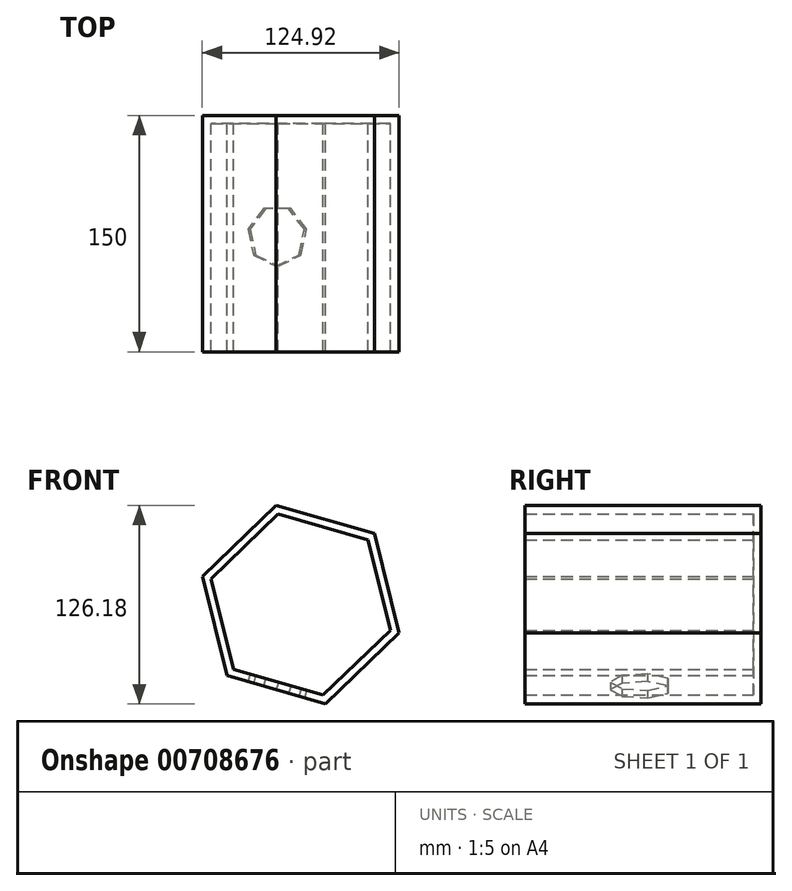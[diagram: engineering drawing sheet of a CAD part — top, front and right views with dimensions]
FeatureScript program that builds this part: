
annotation { "Feature Type Name" : "Feature", "Feature Type Description" : "" }
export const myFeature = defineFeature(function(context is Context, id is Id, definition is map)
    precondition{}
    {
        {
            var Q0;
            Q0=qCreatedBy(makeId("Front.planeOp"),FACE);
            var sketch = newSketch(context, id + "F0", { "sketchPlane" : qUnion([Q0])});
            skCircle(sketch, "E0.cCircle", {"center": v(3.4, 0) * mm, "radius": 56.3 * mm, "construction": true});
            skLineSegment(sketch, "E0.0", {"start": v(-59.06, 17.99) * mm, "end": v(-12.25, 63.09) * mm});
            skLineSegment(sketch, "E0.1", {"start": v(-12.25, 63.09) * mm, "end": v(50.21, 45.1) * mm});
            skLineSegment(sketch, "E0.2", {"start": v(50.21, 45.1) * mm, "end": v(65.86, -17.99) * mm});
            skLineSegment(sketch, "E0.3", {"start": v(65.86, -17.99) * mm, "end": v(19.05, -63.09) * mm});
            skLineSegment(sketch, "E0.4", {"start": v(19.05, -63.09) * mm, "end": v(-43.4, -45.1) * mm});
            skLineSegment(sketch, "E0.5", {"start": v(-43.4, -45.1) * mm, "end": v(-59.06, 17.99) * mm});
            skPoint(sketch, "E0.0.midPoint", {"position": v(-35.65, 40.54) * mm});
            skSolve(sketch);
        }
        {
            var Q0;
            Q0 = qSketchRegion(id + "F0", true);
            extrude(context, id + "F1", {"entities" : qUnion([Q0]), "depth" : 150 * mm, "offsetDistance" : 25.4 * mm});
        }
        {
            var Q0;
            Q0=makeQuery(id+"F1.opExtrude","CAP_FACE",FACE,{"disambiguationData":[OSD([sQuery(id+"F0.wireOp",EDGE,"E0.0"),sQuery(id+"F0.wireOp",EDGE,"E0.1"),sQuery(id+"F0.wireOp",EDGE,"E0.2"),sQuery(id+"F0.wireOp",EDGE,"E0.3"),sQuery(id+"F0.wireOp",EDGE,"E0.4"),sQuery(id+"F0.wireOp",EDGE,"E0.5")])],"isStart":false});
            shell(context, id + "F2", {"entities" : qUnion([Q0]), "thickness" : 5 * mm});
        }
        {
            var Q0;
            Q0=makeQuery(id+"F1.opExtrude","SWEPT_FACE",FACE,{"disambiguationData":[OSD([sQuery(id+"F0.wireOp",EDGE,"E0.4")])]});
            var sketch = newSketch(context, id + "F3", { "sketchPlane" : qUnion([Q0])});
            skCircle(sketch, "E1.cCircle", {"center": v(3.27, 76.46) * mm, "radius": 17.27 * mm, "construction": true});
            skPoint(sketch, "E1.cCircle.centerSnap0", {"position": v(3.27, 150) * mm});
            skLineSegment(sketch, "E1.0", {"start": v(11.59, 59.2) * mm, "end": v(-5.05, 59.2) * mm});
            skLineSegment(sketch, "E1.1", {"start": v(-5.05, 59.2) * mm, "end": v(-15.42, 72.2) * mm});
            skLineSegment(sketch, "E1.2", {"start": v(-15.42, 72.2) * mm, "end": v(-11.72, 88.42) * mm});
            skLineSegment(sketch, "E1.3", {"start": v(-11.72, 88.42) * mm, "end": v(3.27, 95.64) * mm});
            skLineSegment(sketch, "E1.4", {"start": v(3.27, 95.64) * mm, "end": v(18.26, 88.42) * mm});
            skLineSegment(sketch, "E1.5", {"start": v(18.26, 88.42) * mm, "end": v(21.96, 72.2) * mm});
            skLineSegment(sketch, "E1.6", {"start": v(21.96, 72.2) * mm, "end": v(11.59, 59.2) * mm});
            skPoint(sketch, "E1.0.midPoint", {"position": v(3.27, 59.2) * mm});
            skSolve(sketch);
        }
        {
            var Q0;
            Q0 = qSketchRegion(id + "F3", true);
            extrude(context, id + "F4", {"entities" : qUnion([Q0]), "operationType" : NewBodyOperationType.REMOVE, "oppositeDirection" : true, "depth" : 25 * mm, "offsetDistance" : 25 * mm});
        }
    });
